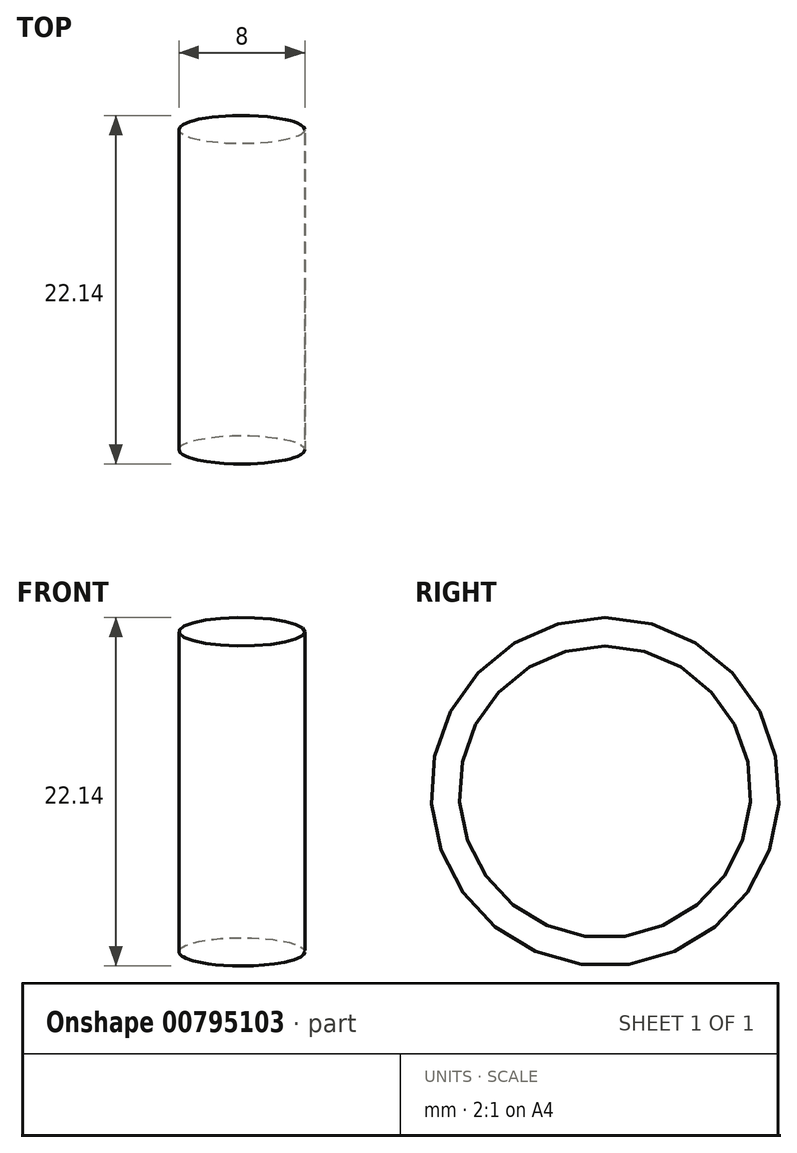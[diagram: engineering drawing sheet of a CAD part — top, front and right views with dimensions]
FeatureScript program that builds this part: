
annotation { "Feature Type Name" : "Feature", "Feature Type Description" : "" }
export const myFeature = defineFeature(function(context is Context, id is Id, definition is map)
    precondition{}
    {
        {
            var Q0;
            Q0=qCreatedBy(makeId("Front.planeOp"),FACE);
            var sketch = newSketch(context, id + "F0", { "sketchPlane" : qUnion([Q0])});
            skLineSegment(sketch, "E0", {"start": v(0, 0) * mm, "end": v(0, 9.26) * mm, "construction": true});
            skLineSegment(sketch, "E1", {"start": v(0, 9.26) * mm, "end": v(0, 10.17) * mm, "construction": true});
            skLineSegment(sketch, "E2", {"start": v(-9.45, 0) * mm, "end": v(19.68, 0) * mm, "construction": true});
            skEllipse(sketch, "E3", {"center": v(0, 10.17) * mm, "majorRadius": 4 * mm, "minorRadius": 0.9 * mm, "majorAxis": v(1, 0)});
            skSolve(sketch);
        }
        {
            var Q0;
            Q0=qCreatedBy(makeId("Front.planeOp"),FACE);
            var sketch = newSketch(context, id + "F1", { "sketchPlane" : qUnion([Q0])});
            skLineSegment(sketch, "E4", {"start": v(-13.08, 0) * mm, "end": v(22.5, 0) * mm});
            skSolve(sketch);
        }
        {
            var Q0;
            Q0=makeQuery(id+"F0.imprint","IMPRINT",FACE,{"disambiguationData":[TD([[makeQuery(id+"F0.imprint","IMPRINT",EDGE,{"derivedFrom":sQuery(id+"F0.wireOp",EDGE,"E3")}),1.0]])]});
            var Q1;
            Q1=sQuery(id+"F1.wireOp",EDGE,"E4");
            revolve(context, id + "F2", {"surfaceOperationType" : NewSurfaceOperationType.NEW, "entities" : qUnion([Q0]), "axis" : qUnion([Q1]), "revolveType" : RevolveType.FULL});
        }
    });
